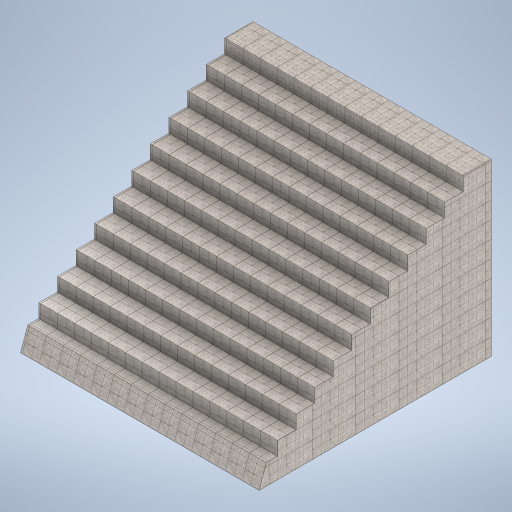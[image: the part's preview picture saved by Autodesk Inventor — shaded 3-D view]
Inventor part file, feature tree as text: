
AUTODESK INVENTOR PART (.ipt)
format: ipt  version: 2024.2 (Build 282272000, 272)  size: 557,568 bytes
history: native  units: mm
features: extrude x3, sketch x3
ambient origin geometry x8: Origin, YZ Plane, XZ Plane, XY Plane, X Axis, Y Axis, Z Axis, Center Point
bodies: Solid1 (feature_tree)
feature tree (6):
  extrude  "Extrusion1"  Depth=2000.0mm
  extrude  "Extrusion2"  Depth=2000.0mm
  extrude  "Extrusion3"  Depth=2800.0mm TaperAngle=0.0deg
  sketch  "Sketch1"  dims[d0=2800.0mm d1=2000.0mm]
  sketch  "Sketch2"  dims[d2=2000.0mm d3=0.0mm d4=19.198622mm]
  sketch  "Sketch3"  dims[d5=2800.0mm d6=0.0mm d7=160.0mm d8=160.0mm d9=160.0mm d10=160.0mm d11=160.0mm d12=160.0mm d13=160.0mm d14=160.0mm d15=160.0mm d16=160.0mm d17=160.0mm d18=160.0mm d19=218.0mm d20=218.0mm d21=218.0mm d22=218.0mm d23=218.0mm d24=218.0mm d25=218.0mm d26=218.0mm d27=218.0mm d28=218.0mm d29=218.0mm d30=218.0mm d31=2800.0mm d32=0.0mm]
